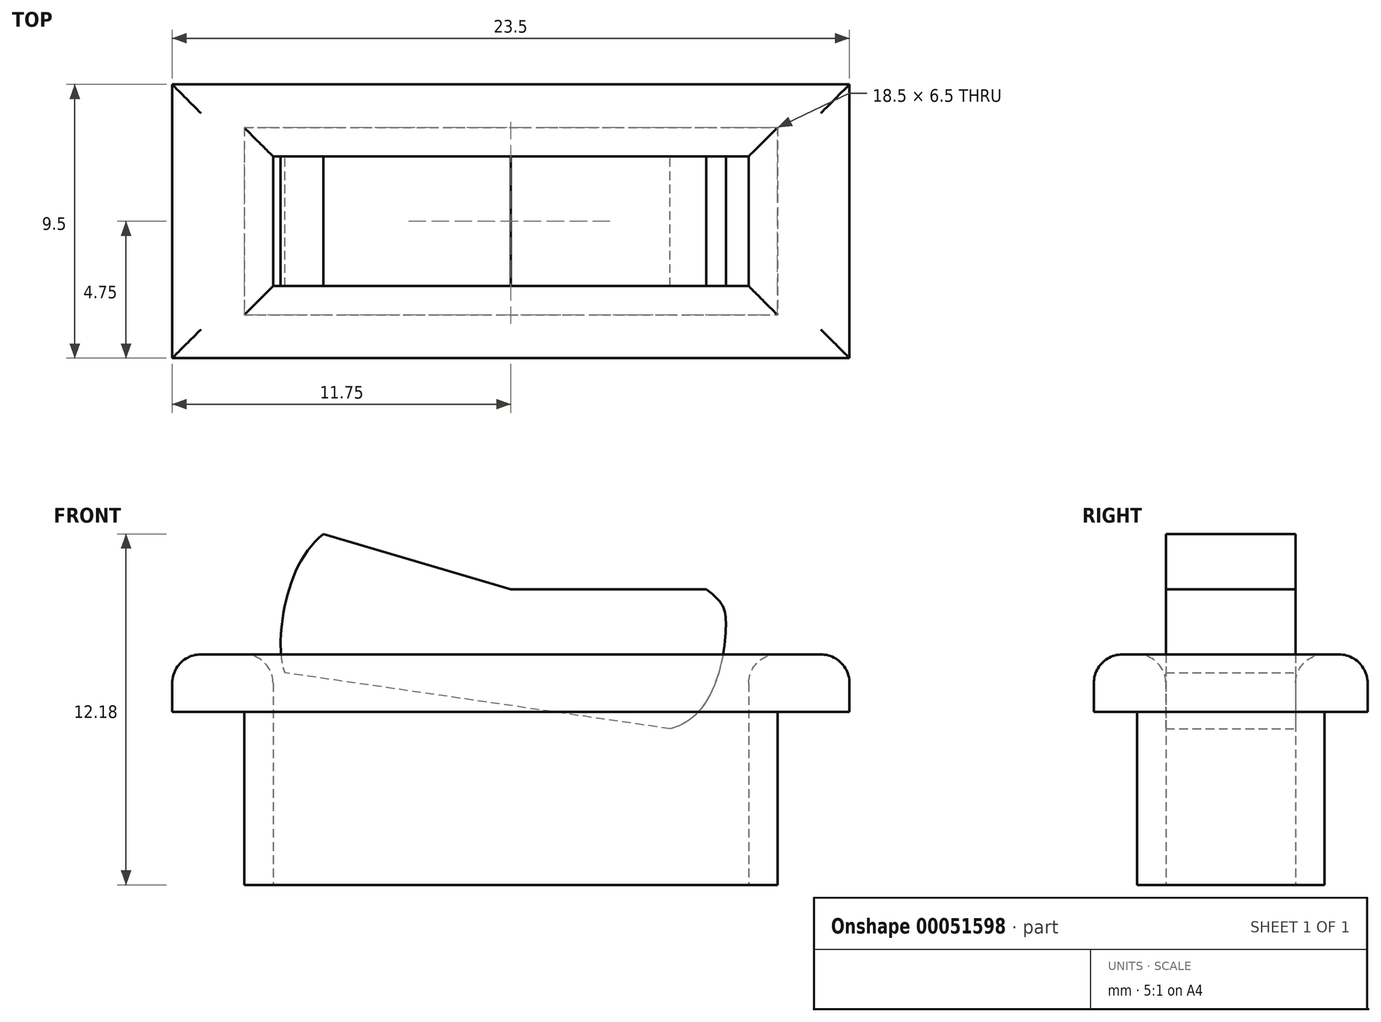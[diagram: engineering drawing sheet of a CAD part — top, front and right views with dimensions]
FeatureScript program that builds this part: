
annotation { "Feature Type Name" : "Feature", "Feature Type Description" : "" }
export const myFeature = defineFeature(function(context is Context, id is Id, definition is map)
    precondition{}
    {
        {
            var Q0;
            Q0=qCreatedBy(makeId("Top.planeOp"),FACE);
            var sketch = newSketch(context, id + "F0", { "sketchPlane" : qUnion([Q0])});
            skLineSegment(sketch, "E0.bottom", {"start": v(-9.25, 3.25) * mm, "end": v(9.25, 3.25) * mm});
            skLineSegment(sketch, "E0.top", {"start": v(-9.25, -3.25) * mm, "end": v(9.25, -3.25) * mm});
            skLineSegment(sketch, "E0.left", {"start": v(-9.25, 3.25) * mm, "end": v(-9.25, -3.25) * mm});
            skLineSegment(sketch, "E0.right", {"start": v(9.25, 3.25) * mm, "end": v(9.25, -3.25) * mm});
            skLineSegment(sketch, "E1.bottom", {"start": v(-8.25, 2.25) * mm, "end": v(8.25, 2.25) * mm});
            skLineSegment(sketch, "E1.top", {"start": v(-8.25, -2.25) * mm, "end": v(8.25, -2.25) * mm});
            skLineSegment(sketch, "E1.left", {"start": v(-8.25, 2.25) * mm, "end": v(-8.25, -2.25) * mm});
            skLineSegment(sketch, "E1.right", {"start": v(8.25, 2.25) * mm, "end": v(8.25, -2.25) * mm});
            skSolve(sketch);
        }
        {
            var Q0;
            Q0=makeQuery(id+"F0.imprint","IMPRINT",FACE,{"disambiguationData":[TD([[makeQuery(id+"F0.imprint","IMPRINT",EDGE,{"derivedFrom":sQuery(id+"F0.wireOp",EDGE,"E0.bottom")}),-1.0]])]});
            extrude(context, id + "F1", {"entities" : qUnion([Q0]), "depth" : 6 * mm});
        }
        {
            var Q0;
            Q0=makeQuery(id+"F1.opExtrude","CAP_FACE",FACE,{"disambiguationData":[OSD([sQuery(id+"F0.wireOp",EDGE,"E0.bottom"),sQuery(id+"F0.wireOp",EDGE,"E0.top"),sQuery(id+"F0.wireOp",EDGE,"E0.left"),sQuery(id+"F0.wireOp",EDGE,"E0.right"),sQuery(id+"F0.wireOp",EDGE,"E1.bottom"),sQuery(id+"F0.wireOp",EDGE,"E1.top"),sQuery(id+"F0.wireOp",EDGE,"E1.left"),sQuery(id+"F0.wireOp",EDGE,"E1.right")])],"isStart":false});
            var sketch = newSketch(context, id + "F2", { "sketchPlane" : qUnion([Q0])});
            skLineSegment(sketch, "E2.bottom", {"start": v(-11.75, 4.75) * mm, "end": v(11.75, 4.75) * mm});
            skLineSegment(sketch, "E2.top", {"start": v(-11.75, -4.75) * mm, "end": v(11.75, -4.75) * mm});
            skLineSegment(sketch, "E2.left", {"start": v(-11.75, 4.75) * mm, "end": v(-11.75, -4.75) * mm});
            skLineSegment(sketch, "E2.right", {"start": v(11.75, 4.75) * mm, "end": v(11.75, -4.75) * mm});
            skSolve(sketch);
        }
        {
            var Q0;
            Q0=makeQuery(id+"F2.imprint","IMPRINT",FACE,{"disambiguationData":[TD([[makeQuery(id+"F2.imprint","IMPRINT",EDGE,{"derivedFrom":sQuery(id+"F2.wireOp",EDGE,"E2.bottom")}),-1.0]])]});
            var Q1;
            Q1=makeQuery(id+"F2.imprint","IMPRINT",FACE,{"disambiguationData":[TD([[makeQuery(id+"F2.imprint","IMPRINT",EDGE,{"derivedFrom":makeQuery(id+"F1.opExtrude","CAP_EDGE",EDGE,{"disambiguationData":[OSD([sQuery(id+"F0.wireOp",EDGE,"E0.bottom")])],"isStart":false})}),-1.0]])]});
            extrude(context, id + "F3", {"entities" : qUnion([Q0, Q1]), "operationType" : NewBodyOperationType.ADD, "depth" : 2 * mm});
        }
        {
            var Q0;
            {var subQ0=sQuery(id+"F0.wireOp",EDGE,"E1.bottom");Q0=makeQuery(id+"F3.boolean.opBoolean","MERGE",FACE,{"derivedFrom":[makeQuery(id+"F1.opExtrude","SWEPT_FACE",FACE,{"disambiguationData":[OSD([subQ0])]}),makeQuery(id+"F3.opExtrude","SWEPT_FACE",FACE,{"disambiguationData":[OSD([subQ0])]})]});}
            var sketch = newSketch(context, id + "F4", { "sketchPlane" : qUnion([Q0])});
            skLineSegment(sketch, "E3", {"start": v(0, 10.26) * mm, "end": v(-6.5, 12.18) * mm});
            skLineSegment(sketch, "E4", {"start": v(0, 10.26) * mm, "end": v(6.78, 10.26) * mm});
            skFitSpline(sketch, "E5", {"points": [v(-6.5, 12.18) * mm, v(-7.83, 7.36) * mm], "startDerivative": vector(-4.53, -3.45) * mm, "endDerivative": vector(1.05, -1.93) * mm});
            skFitSpline(sketch, "E6", {"points": [v(6.78, 10.26) * mm, v(7.46, 9) * mm, v(5.53, 5.42) * mm], "startDerivative": vector(4.76, -3.65) * mm, "endDerivative": vector(-7.52, -1.76) * mm});
            skLineSegment(sketch, "E7", {"start": v(-7.83, 7.36) * mm, "end": v(5.53, 5.42) * mm});
            skSolve(sketch);
        }
        {
            var Q0;
            {var subQ5=sQuery(id+"F4.wireOp",EDGE,"E3");Q0=makeQuery(id+"F4.imprint","IMPRINT",FACE,{"disambiguationData":[TD([[makeQuery(id+"F4.imprint","IMPRINT",EDGE,{"derivedFrom":subQ5}),1.0]])]});}
            var Q1;
            {var subQ0=sQuery(id+"F4.wireOp",EDGE,"E7");Q1=makeQuery(id+"F4.imprint","IMPRINT",FACE,{"disambiguationData":[TD([[makeQuery(id+"F4.imprint","IMPRINT",EDGE,{"derivedFrom":subQ0}),1.0]])]});}
            var Q2;
            {var subQ0=sQuery(id+"F0.wireOp",EDGE,"E1.top");Q2=makeQuery(id+"F3.boolean.opBoolean","MERGE",FACE,{"derivedFrom":[makeQuery(id+"F1.opExtrude","SWEPT_FACE",FACE,{"disambiguationData":[OSD([subQ0])]}),makeQuery(id+"F3.opExtrude","SWEPT_FACE",FACE,{"disambiguationData":[OSD([subQ0])]})]});}
            extrude(context, id + "F5", {"entities" : qUnion([Q0, Q1]), "endBound" : BoundingType.UP_TO_SURFACE, "endBoundEntityFace" : qUnion([Q2]), "depth" : 25 * mm});
        }
        {
            var Q0;
            Q0=makeQuery(id+"F3.opExtrude","CAP_FACE",FACE,{"disambiguationData":[OSD([sQuery(id+"F0.wireOp",EDGE,"E1.bottom"),sQuery(id+"F0.wireOp",EDGE,"E1.top"),sQuery(id+"F0.wireOp",EDGE,"E1.left"),sQuery(id+"F0.wireOp",EDGE,"E1.right"),sQuery(id+"F2.wireOp",EDGE,"E2.bottom"),sQuery(id+"F2.wireOp",EDGE,"E2.top"),sQuery(id+"F2.wireOp",EDGE,"E2.left"),sQuery(id+"F2.wireOp",EDGE,"E2.right")])],"isStart":false});
            fillet(context, id + "F6", {"entities" : qUnion([Q0]), "radius" : 1 * mm, "tangentPropagation" : true, "allowEdgeOverflow" : false});
        }
    });
